# Revit family: Differential Pressure Control Valve 4007 FIX WE 23kPa
name_source: partatom
category: Rohrzubehör
revit_build: Autodesk Revit 2018 (Build: 20190510_1515(x64)
units: mm (PartAtom-declared; Revit-internal decimal feet)

## family parameters
Arbeitsebenenbasiert = Nein
Beim Laden mit Abzugskörper schneiden = Nein
Bemaßung runder Anschluss = Durchmesser verwenden
Gemeinsam genutzt = Nein
Immer vertikal = Ja
OmniClass-Nummer = 23.65.55.14.24
OmniClass-Titel = Mixing Valves for Liquid Services
Teiletyp = Unterbricht

## types (1)
- Differential Pressure Control Valve 4007 FIX WE 23kPa
    Application = For heating and cooling systems, to ensure constant differential pressure constant within the
control range.
Reset from HERZ STROMAX circuit regulating valves.
    Hersteller = HERZ-Armaturen Ges.m.b.H
    Materials = Ammonia contained in hemp can damage brass valve bodies, EPDM gaskets can be affected by
mineral oil lubricants and thus lead to failure of the EPDM seals. Please refer to manufacturers
documentation when using ethylene glycol products for frost and corrosion protection.
    Max. differential pressure on the body = 250000.0 Pa
    Max. operating pressure = 1000000.0 Pa
    Max. operating temperature = 95 °C
    Medium = Ethylene and propylene glycol is to be used in a mixing ratio of 25 - 50 Vol. [%].
Water quality according to ONORM H 5195 and VDI 2035
    Membrane and O-Rings = EPDM
    Min. operating temperature (frost protection) = -10 °C
    Min. operating temperature (frost protection, brass body) = -20 °C
    Min. operating temperature (pure water) = 2 °C
    Model = The differential pressure controller is a straight-version proportional controller and works without auxiliary energy.
Differential pressure 23 kPa permanently set. The impulse line (1000 mm) is included with the valve and is connected to a
circuit regulating valve in the supply line.
    SCRNCODE = 05;03;4
    SCRNSEQ = ARM;ARM_TYP="DIFR";2
    Set point spring = stainless steel
    URL = www.herzvalves.com
    Valve body = dezincification-resistant brass
    a1 = 9.5 mm  [stored 0.031168 ft]
    a2 = 21.02 mm
    a3 = 9.5 mm  [stored 0.031168 ft]
    h1 = 20.59 mm
    k1 = 21 mm  [stored 0.0688976 ft]
    k10 = 20.56 mm  [stored 0.0674541 ft]
    k11 = 45 mm  [stored 0.147638 ft]
    k12 = 39.28 mm
    k13 = 14 mm  [stored 0.0459318 ft]
    k14 = 101.66 mm
    k16 = 7.28 mm  [stored 0.0238845 ft]
    k18 = 24.47 mm
    k19 = 24.47 mm
    k2 = 49.08 mm  [stored 0.161024 ft]
    k20 = 70.56 mm
    k21 = 28.72 mm
    k22 = 3.22 mm
    k3 = 63 mm  [stored 0.206693 ft]
    k4 = 142.00°
    k5 = 11.83 mm
    k6 = 8.68 mm
    k7 = 9.45 mm
    k8 = 130.00°
    k9 = 17.65 mm
    m1 = 3.5 mm  [stored 0.0114829 ft]
    m3 = 4 mm  [stored 0.0131234 ft]
    t1 = 24.47 mm

note: [stored X ft] marks values corroborated as IEEE doubles in the binary element streams (Revit-internal decimal feet)
